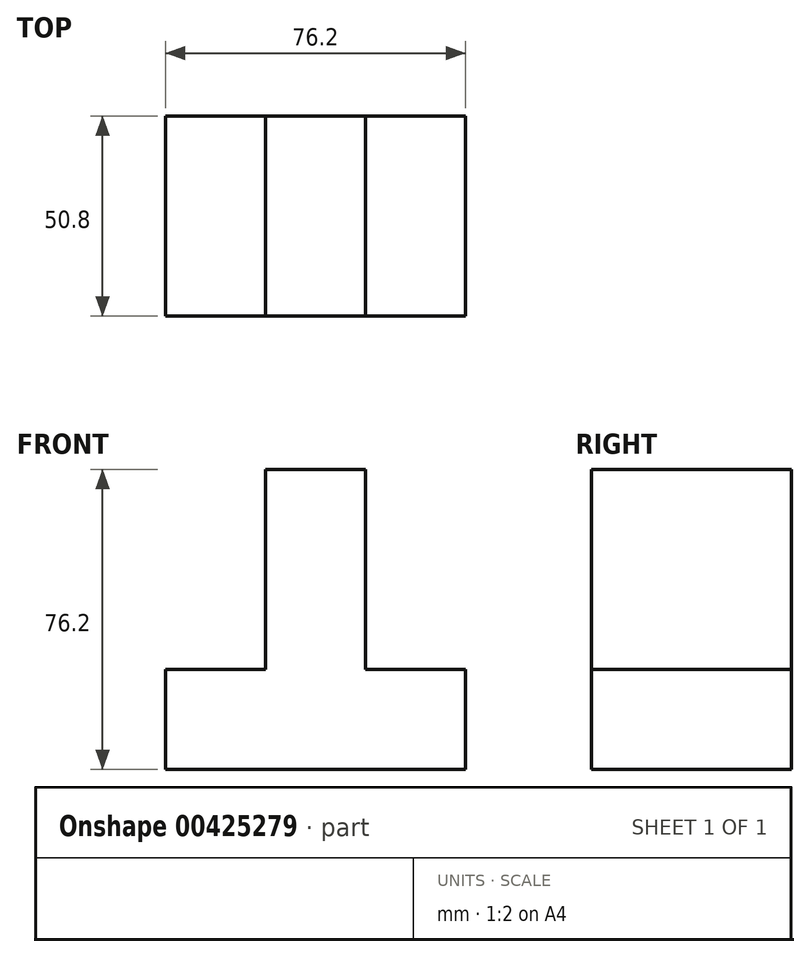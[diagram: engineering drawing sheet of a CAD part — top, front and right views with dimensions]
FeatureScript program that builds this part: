
annotation { "Feature Type Name" : "Feature", "Feature Type Description" : "" }
export const myFeature = defineFeature(function(context is Context, id is Id, definition is map)
    precondition{}
    {
        {
            var Q0;
            Q0=qCreatedBy(makeId("Front.planeOp"),FACE);
            var sketch = newSketch(context, id + "F0", { "sketchPlane" : qUnion([Q0])});
            skLineSegment(sketch, "E0", {"start": v(-50.8, 70.09) * mm, "end": v(-50.8, 19.29) * mm});
            skLineSegment(sketch, "E1", {"start": v(-50.8, 19.29) * mm, "end": v(-76.2, 19.29) * mm});
            skLineSegment(sketch, "E2", {"start": v(-76.2, 19.29) * mm, "end": v(-76.2, -6.11) * mm});
            skLineSegment(sketch, "E3", {"start": v(-76.2, -6.11) * mm, "end": v(0, -6.11) * mm});
            skLineSegment(sketch, "E4", {"start": v(0, -6.11) * mm, "end": v(0, 19.29) * mm});
            skLineSegment(sketch, "E5", {"start": v(0, 19.29) * mm, "end": v(-25.4, 19.29) * mm});
            skLineSegment(sketch, "E6", {"start": v(-25.4, 19.29) * mm, "end": v(-25.4, 70.09) * mm});
            skLineSegment(sketch, "E7", {"start": v(-25.4, 70.09) * mm, "end": v(-50.8, 70.09) * mm});
            skSolve(sketch);
        }
        {
            var Q0;
            Q0 = qSketchRegion(id + "F0", true);
            extrude(context, id + "F1", {"entities" : qUnion([Q0]), "depth" : 50.8 * mm});
        }
    });
